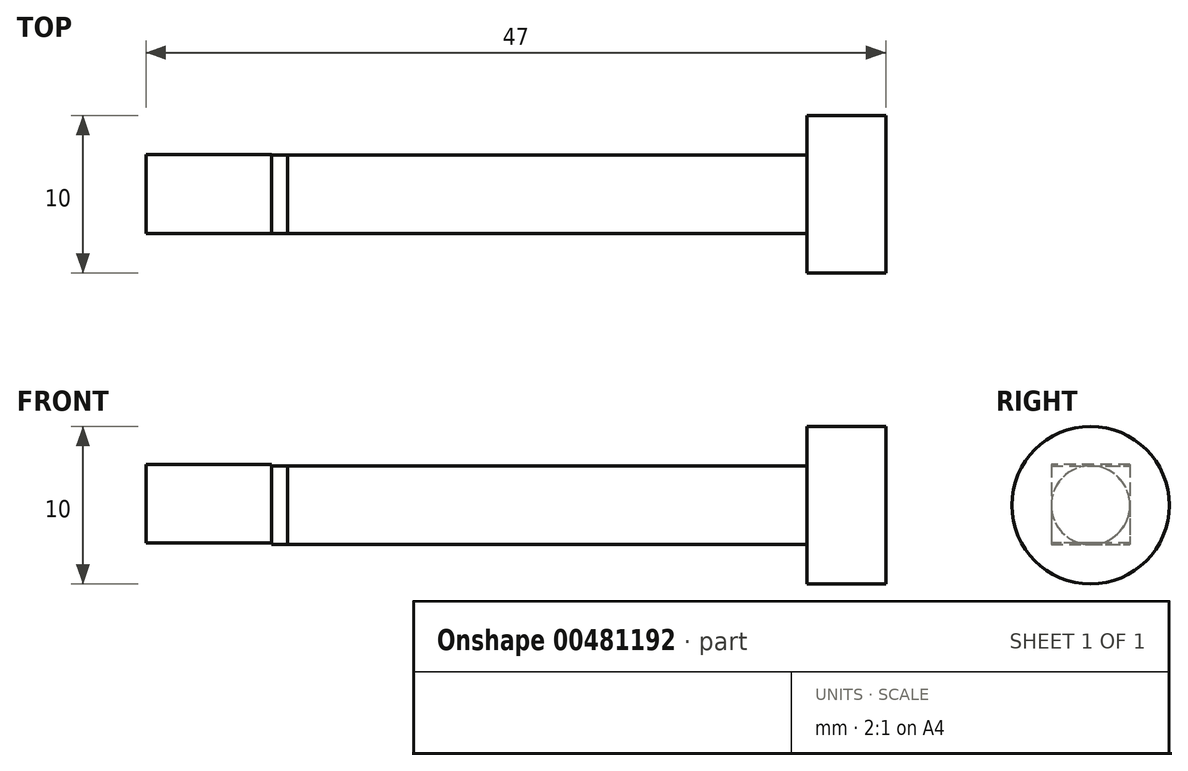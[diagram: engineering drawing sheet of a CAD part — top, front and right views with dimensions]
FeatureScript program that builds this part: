
annotation { "Feature Type Name" : "Feature", "Feature Type Description" : "" }
export const myFeature = defineFeature(function(context is Context, id is Id, definition is map)
    precondition{}
    {
        {
            var Q0;
            Q0=qCreatedBy(makeId("Right.planeOp"),FACE);
            var sketch = newSketch(context, id + "F0", { "sketchPlane" : qUnion([Q0])});
            skLineSegment(sketch, "E0.bottom", {"start": v(-2.5, -2.5) * mm, "end": v(2.5, -2.5) * mm});
            skLineSegment(sketch, "E0.top", {"start": v(-2.5, 2.5) * mm, "end": v(2.5, 2.5) * mm});
            skLineSegment(sketch, "E0.left", {"start": v(-2.5, 2.5) * mm, "end": v(-2.5, -2.5) * mm});
            skLineSegment(sketch, "E0.right", {"start": v(2.5, 2.5) * mm, "end": v(2.5, -2.5) * mm});
            skSolve(sketch);
        }
        {
            var Q0;
            Q0 = qSketchRegion(id + "F0", true);
            extrude(context, id + "F1", {"entities" : qUnion([Q0]), "depth" : 33 * mm});
        }
        {
            var Q0;
            Q0=makeQuery(id+"F1.opExtrude","CAP_FACE",FACE,{"disambiguationData":[OSD([sQuery(id+"F0.wireOp",EDGE,"E0.bottom"),sQuery(id+"F0.wireOp",EDGE,"E0.top"),sQuery(id+"F0.wireOp",EDGE,"E0.left"),sQuery(id+"F0.wireOp",EDGE,"E0.right")])],"isStart":false});
            var sketch = newSketch(context, id + "F2", { "sketchPlane" : qUnion([Q0])});
            skCircle(sketch, "E1", {"center": v(0, 0) * mm, "radius": 5 * mm});
            skSolve(sketch);
        }
        {
            var Q0;
            Q0 = qSketchRegion(id + "F2", true);
            extrude(context, id + "F3", {"entities" : qUnion([Q0]), "operationType" : NewBodyOperationType.ADD, "depth" : 5 * mm});
        }
        {
            var Q0;
            Q0=makeQuery(id+"F1.opExtrude","CAP_FACE",FACE,{"disambiguationData":[OSD([sQuery(id+"F0.wireOp",EDGE,"E0.bottom"),sQuery(id+"F0.wireOp",EDGE,"E0.top"),sQuery(id+"F0.wireOp",EDGE,"E0.left"),sQuery(id+"F0.wireOp",EDGE,"E0.right")])],"isStart":true});
            var sketch = newSketch(context, id + "F4", { "sketchPlane" : qUnion([Q0])});
            skCircle(sketch, "E2", {"center": v(0, 0) * mm, "radius": 2.5 * mm});
            skSolve(sketch);
        }
        {
            var Q0;
            {var subQ0=sQuery(id+"F4.wireOp",EDGE,"E2");var subQ1=makeQuery(id+"F4.imprint","INTERSECT",VERTEX,{"derivedFrom":[makeQuery(id+"F1.opExtrude","CAP_EDGE",EDGE,{"disambiguationData":[OSD([sQuery(id+"F0.wireOp",EDGE,"E0.top")])],"isStart":true}),subQ0]});Q0=makeQuery(id+"F4.imprint","IMPRINT",FACE,{"disambiguationData":[TD([[makeQuery(id+"F4.imprint","IMPRINT",EDGE,{"disambiguationData":[TD([[subQ1,1.0]])],"derivedFrom":subQ0}),1.0]])]});}
            extrude(context, id + "F5", {"entities" : qUnion([Q0]), "operationType" : NewBodyOperationType.ADD, "depth" : 1 * mm});
        }
        {
            var Q0;
            Q0=makeQuery(id+"F5.opExtrude","CAP_FACE",FACE,{"disambiguationData":[OSD([sQuery(id+"F4.wireOp",EDGE,"E2")])],"isStart":false});
            var sketch = newSketch(context, id + "F6", { "sketchPlane" : qUnion([Q0])});
            skLineSegment(sketch, "E3.bottom", {"start": v(-2.51, 2.54) * mm, "end": v(2.49, 2.54) * mm});
            skLineSegment(sketch, "E3.top", {"start": v(-2.51, -2.46) * mm, "end": v(2.49, -2.46) * mm});
            skLineSegment(sketch, "E3.left", {"start": v(-2.51, 2.54) * mm, "end": v(-2.51, -2.46) * mm});
            skLineSegment(sketch, "E3.right", {"start": v(2.49, 2.54) * mm, "end": v(2.49, -2.46) * mm});
            skSolve(sketch);
        }
        {
            var Q0;
            {var subQ0=sQuery(id+"F6.wireOp",EDGE,"E3.top");var subQ1=makeQuery(id+"F5.opExtrude","CAP_EDGE",EDGE,{"disambiguationData":[OSD([sQuery(id+"F4.wireOp",EDGE,"E2")])],"isStart":false});var subQ2=makeQuery(id+"F6.imprint","INTERSECT",VERTEX,{"disambiguationData":[OD(0.0)],"derivedFrom":[subQ1,subQ0]});Q0=makeQuery(id+"F6.imprint","IMPRINT",FACE,{"disambiguationData":[TD([[makeQuery(id+"F6.imprint","IMPRINT",EDGE,{"disambiguationData":[TD([[subQ2,-1.0]])],"derivedFrom":subQ0}),1.0]])]});}
            var sketch = newSketch(context, id + "F7", { "sketchPlane" : qUnion([Q0])});
            skLineSegment(sketch, "E4.bottom", {"start": v(-2.51, 2.6) * mm, "end": v(2.49, 2.6) * mm});
            skLineSegment(sketch, "E4.top", {"start": v(-2.51, -2.4) * mm, "end": v(2.49, -2.4) * mm});
            skLineSegment(sketch, "E4.left", {"start": v(-2.51, 2.6) * mm, "end": v(-2.51, -2.4) * mm});
            skLineSegment(sketch, "E4.right", {"start": v(2.49, 2.6) * mm, "end": v(2.49, -2.4) * mm});
            skSolve(sketch);
        }
        {
            var Q0;
            Q0 = qSketchRegion(id + "F7", true);
            extrude(context, id + "F8", {"entities" : qUnion([Q0]), "operationType" : NewBodyOperationType.ADD, "depth" : 8 * mm});
        }
    });
